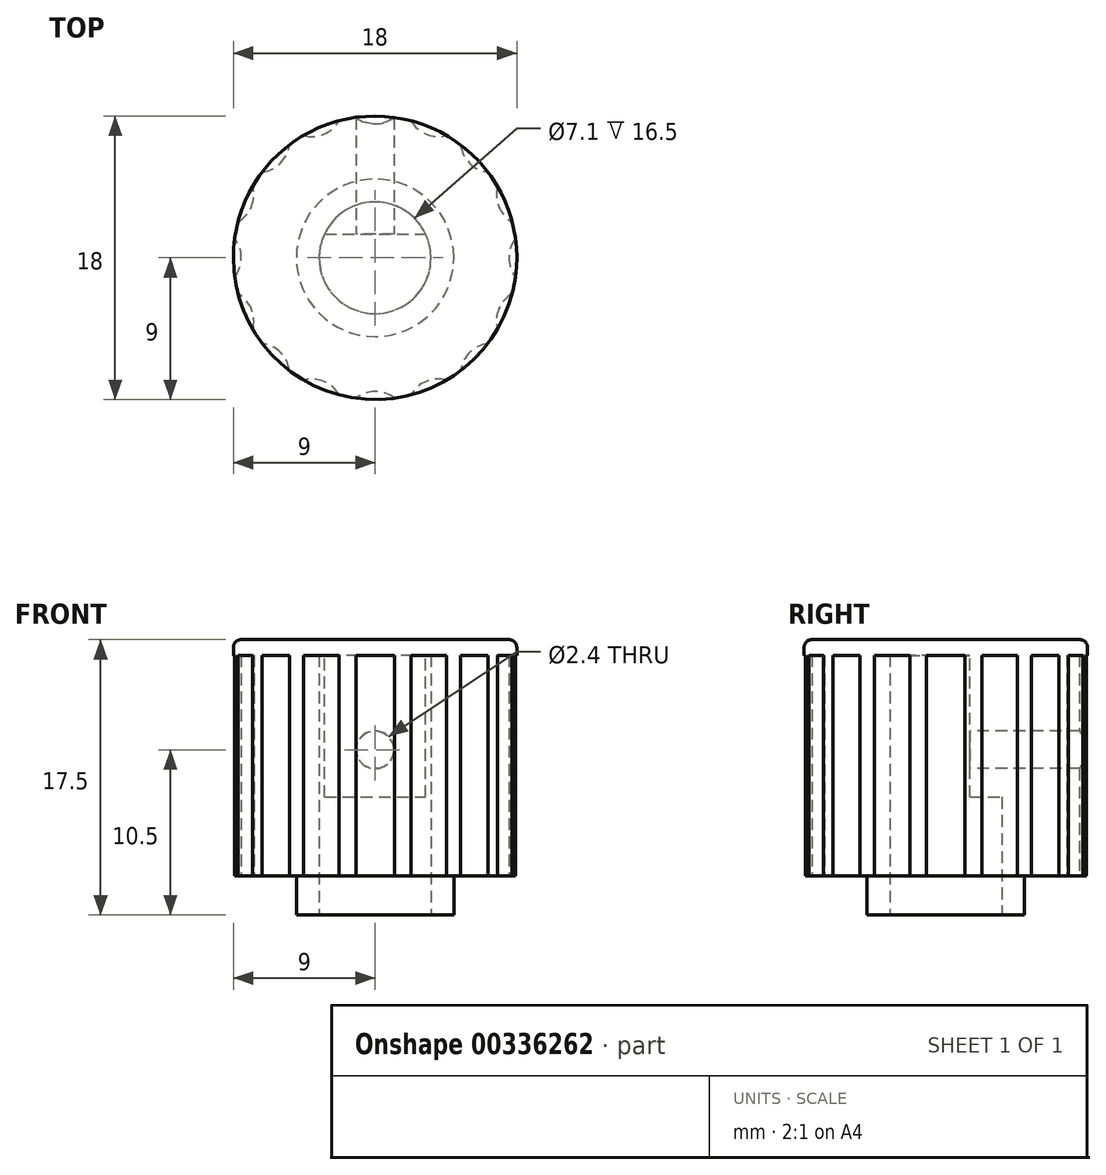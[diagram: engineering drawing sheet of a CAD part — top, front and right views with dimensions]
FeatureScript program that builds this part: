
annotation { "Feature Type Name" : "Feature", "Feature Type Description" : "" }
export const myFeature = defineFeature(function(context is Context, id is Id, definition is map)
    precondition{}
    {
        {
            var Q0;
            Q0=qCreatedBy(makeId("Front.planeOp"),FACE);
            var sketch = newSketch(context, id + "F0", { "sketchPlane" : qUnion([Q0])});
            skLineSegment(sketch, "E0", {"start": v(0, -2.23) * mm, "end": v(0, -5.1) * mm, "construction": true});
            skLineSegment(sketch, "E1", {"start": v(0, 0) * mm, "end": v(-5, 0) * mm});
            skLineSegment(sketch, "E2", {"start": v(-5, 0) * mm, "end": v(-5, 2.5) * mm});
            skLineSegment(sketch, "E3", {"start": v(-5, 2.5) * mm, "end": v(-9, 2.5) * mm});
            skLineSegment(sketch, "E4", {"start": v(-9, 2.5) * mm, "end": v(-9, 17.5) * mm});
            skLineSegment(sketch, "E5", {"start": v(-9, 17.5) * mm, "end": v(0, 17.5) * mm});
            skLineSegment(sketch, "E6", {"start": v(0, 0) * mm, "end": v(0, 17.5) * mm});
            skSolve(sketch);
        }
        {
            var Q0;
            Q0=qSketchRegion(id+"F0",true);
            var Q1;
            Q1=sQuery(id+"F0.wireOp",EDGE,"E0");
            revolve(context, id + "F1", {"entities" : qUnion([Q0]), "axis" : qUnion([Q1]), "revolveType" : RevolveType.FULL});
        }
        {
            var Q0;
            Q0=makeQuery(id+"F1.opRevolve","SWEPT_FACE",FACE,{"disambiguationData":[OSD([sQuery(id+"F0.wireOp",EDGE,"E1")])]});
            var sketch = newSketch(context, id + "F2", { "sketchPlane" : qUnion([Q0])});
            skCircle(sketch, "E7", {"center": v(0, 0) * mm, "radius": 3.55 * mm});
            skSolve(sketch);
        }
        {
            var Q0;
            Q0=qSketchRegion(id+"F2",true);
            extrude(context, id + "F3", {"entities" : qUnion([Q0]), "operationType" : NewBodyOperationType.REMOVE, "oppositeDirection" : true, "depth" : 16.5 * mm});
        }
        {
            var Q0;
            Q0=makeQuery(id+"F3.boolean.opBoolean","COPY",FACE,{"derivedFrom":makeQuery(id+"F3.opExtrude","CAP_FACE",FACE,{"disambiguationData":[OSD([sQuery(id+"F2.wireOp",EDGE,"E7")])],"isStart":false})});
            var sketch = newSketch(context, id + "F4", { "sketchPlane" : qUnion([Q0])});
            skArc(sketch, "E8", {"start": v(-3.2, -1.52) * mm, "mid": v(0, -3.55) * mm, "end": v(3.2, -1.52) * mm});
            skLineSegment(sketch, "E9", {"start": v(-3.2, -1.52) * mm, "end": v(3.2, -1.52) * mm});
            skSolve(sketch);
        }
        {
            var Q0;
            Q0=qSketchRegion(id+"F4",true);
            extrude(context, id + "F5", {"entities" : qUnion([Q0]), "operationType" : NewBodyOperationType.ADD, "depth" : 9 * mm});
        }
        {
            var Q0;
            Q0=makeQuery(id+"F1.opRevolve","SWEPT_EDGE",EDGE,{"disambiguationData":[OSD([sQuery(id+"F0.wireOp",EDGE,"E4"),sQuery(id+"F0.wireOp",EDGE,"E5")])]});
            fillet(context, id + "F6", {"entities" : qUnion([Q0]), "radius" : 0.5 * mm, "tangentPropagation" : true, "allowEdgeOverflow" : false});
        }
        {
            var Q0;
            Q0=makeQuery(id+"F5.opExtrude","SWEPT_FACE",FACE,{"disambiguationData":[OSD([sQuery(id+"F4.wireOp",EDGE,"E9")])]});
            var sketch = newSketch(context, id + "F7", { "sketchPlane" : qUnion([Q0])});
            skCircle(sketch, "E10", {"center": v(0, 10.5) * mm, "radius": 1.2 * mm});
            skSolve(sketch);
        }
        {
            var Q0;
            Q0 = qSketchRegion(id + "F7", true);
            extrude(context, id + "F8", {"entities" : qUnion([Q0]), "operationType" : NewBodyOperationType.REMOVE, "oppositeDirection" : true, "depth" : 10 * mm});
        }
        {
            var Q0;
            Q0=makeQuery(id+"F1.opRevolve","SWEPT_FACE",FACE,{"disambiguationData":[OSD([sQuery(id+"F0.wireOp",EDGE,"E3")])]});
            var sketch = newSketch(context, id + "F9", { "sketchPlane" : qUnion([Q0])});
            skCircle(sketch, "E11", {"center": v(-10.5, 0) * mm, "radius": 2 * mm});
            skCircle(sketch, "E12.1.0", {"center": v(-9.7, -4.02) * mm, "radius": 2 * mm});
            skCircle(sketch, "E12.2.0", {"center": v(-7.42, -7.42) * mm, "radius": 2 * mm});
            skCircle(sketch, "E12.3.0", {"center": v(-4.02, -9.7) * mm, "radius": 2 * mm});
            skCircle(sketch, "E12.4.0", {"center": v(0, -10.5) * mm, "radius": 2 * mm});
            skCircle(sketch, "E12.5.0", {"center": v(4.02, -9.7) * mm, "radius": 2 * mm});
            skCircle(sketch, "E12.6.0", {"center": v(7.42, -7.42) * mm, "radius": 2 * mm});
            skCircle(sketch, "E12.7.0", {"center": v(9.7, -4.02) * mm, "radius": 2 * mm});
            skCircle(sketch, "E12.8.0", {"center": v(10.5, 0) * mm, "radius": 2 * mm});
            skCircle(sketch, "E12.9.0", {"center": v(9.7, 4.02) * mm, "radius": 2 * mm});
            skCircle(sketch, "E12.10.0", {"center": v(7.42, 7.42) * mm, "radius": 2 * mm});
            skCircle(sketch, "E12.11.0", {"center": v(4.02, 9.7) * mm, "radius": 2 * mm});
            skCircle(sketch, "E12.12.0", {"center": v(0, 10.5) * mm, "radius": 2 * mm});
            skCircle(sketch, "E12.13.0", {"center": v(-4.02, 9.7) * mm, "radius": 2 * mm});
            skCircle(sketch, "E12.14.0", {"center": v(-7.42, 7.42) * mm, "radius": 2 * mm});
            skCircle(sketch, "E12.15.0", {"center": v(-9.7, 4.02) * mm, "radius": 2 * mm});
            skPoint(sketch, "E12.center", {"position": v(0, 0) * mm});
            skSolve(sketch);
        }
        {
            var Q0;
            Q0 = qSketchRegion(id + "F9", true);
            extrude(context, id + "F10", {"entities" : qUnion([Q0]), "operationType" : NewBodyOperationType.REMOVE, "oppositeDirection" : true, "depth" : 14 * mm});
        }
    });
